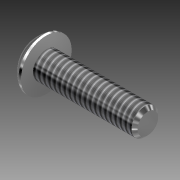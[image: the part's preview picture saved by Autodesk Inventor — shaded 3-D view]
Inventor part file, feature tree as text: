
AUTODESK INVENTOR PART (.ipt)
format: ipt  version: 2011 (Build 150239000, 239)  size: 115,712 bytes
history: native  units: in
note: dims shown in document units (in); Inventor stores cm internally (conversion verified against a paired STEP export)
features: other x1, imported_body x1, thread x1
ambient origin geometry x8: Origin, YZ Plane, XZ Plane, XY Plane, X Axis, Y Axis, Z Axis, Center Point
feature tree (3):
  parser-record x1  (decoder bookkeeping rows leaked as tree rows — omitted from the tree; the rows remain in map.json)
  imported_body  "Base1"
  thread  "Thread1"  [1 undecoded]
note: 1 required parameter value undecoded (feature->parameter linkage not recoverable at this tier; creation-order binding heuristic only, values carry confidence <= 0.55)
